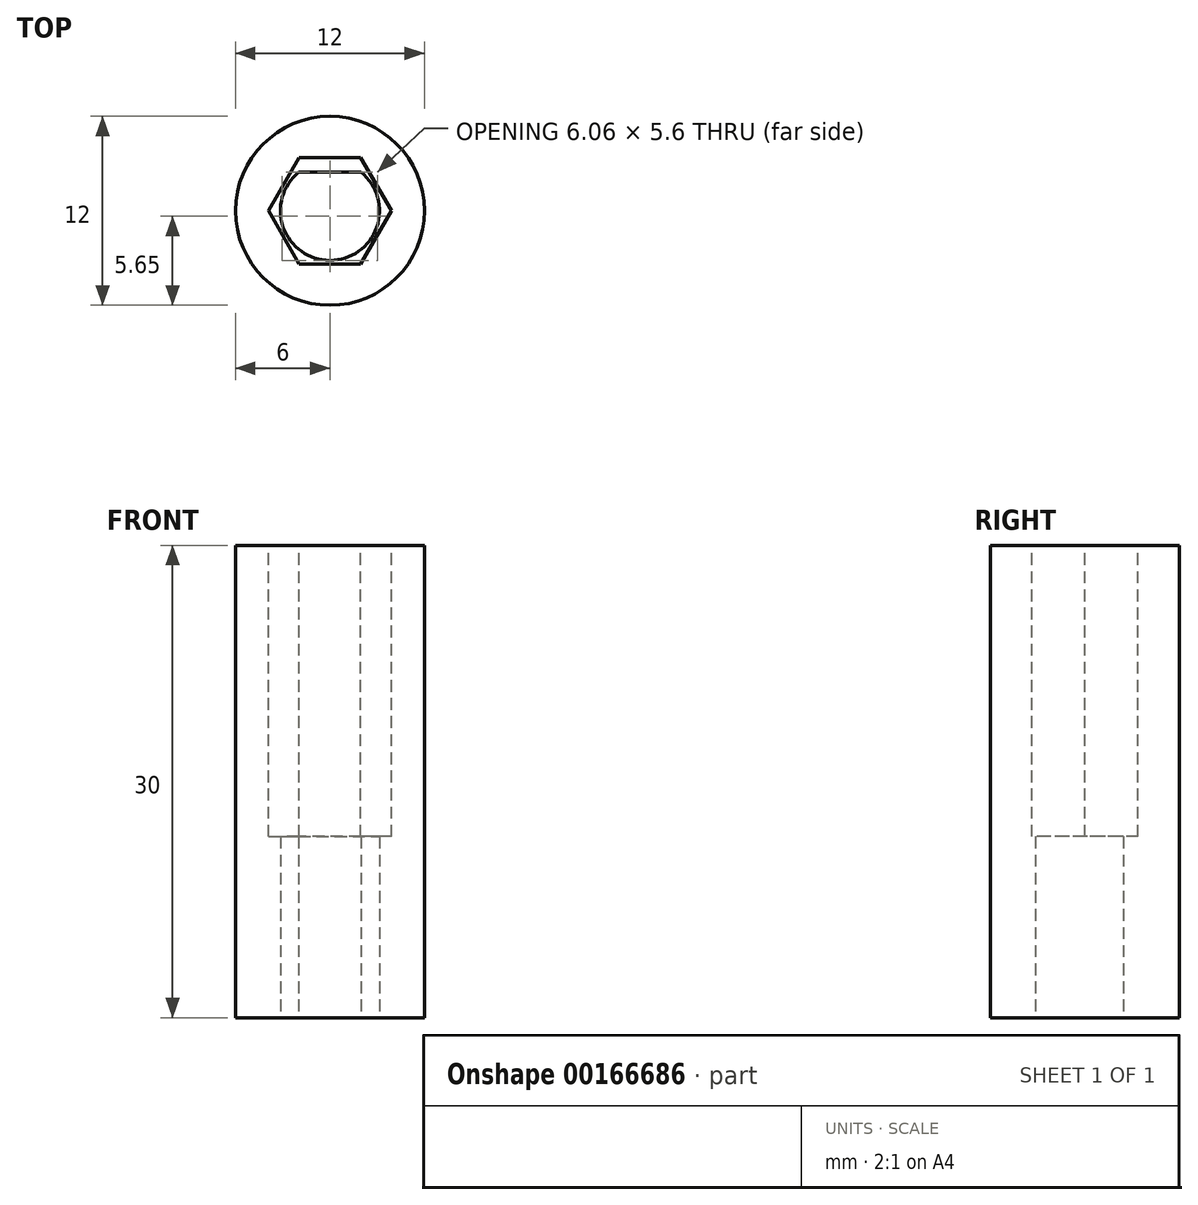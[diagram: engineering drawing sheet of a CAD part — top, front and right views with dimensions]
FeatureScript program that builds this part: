
annotation { "Feature Type Name" : "Feature", "Feature Type Description" : "" }
export const myFeature = defineFeature(function(context is Context, id is Id, definition is map)
    precondition{}
    {
        {
            var Q0;
            Q0=qCreatedBy(makeId("Top.planeOp"),FACE);
            var sketch = newSketch(context, id + "F0", { "sketchPlane" : qUnion([Q0])});
            skCircle(sketch, "E0", {"center": v(0, 0) * mm, "radius": 6 * mm});
            skSolve(sketch);
        }
        {
            var Q0;
            Q0 = qSketchRegion(id + "F0", true);
            extrude(context, id + "F1", {"entities" : qUnion([Q0]), "depth" : 30 * mm, "symmetric" : true});
        }
        {
            var Q0;
            Q0=makeQuery(id+"F1.opExtrude","CAP_FACE",FACE,{"disambiguationData":[OSD([sQuery(id+"F0.wireOp",EDGE,"E0")])],"isStart":true});
            var sketch = newSketch(context, id + "F2", { "sketchPlane" : qUnion([Q0])});
            skArc(sketch, "E1", {"start": v(1.98, -2.45) * mm, "mid": v(0, 3.15) * mm, "end": v(-1.98, -2.45) * mm});
            skLineSegment(sketch, "E2", {"start": v(-1.98, -2.45) * mm, "end": v(1.98, -2.45) * mm});
            skSolve(sketch);
        }
        {
            var Q0;
            Q0 = qSketchRegion(id + "F2", true);
            var Q1;
            Q1=sQuery(id+"F2.wireOp",EDGE,"E1");
            extrude(context, id + "F3", {"entities" : qUnion([Q0]), "operationType" : NewBodyOperationType.REMOVE, "surfaceEntities" : qUnion([Q1]), "oppositeDirection" : true, "depth" : 12 * mm});
        }
        {
            var Q0;
            Q0=makeQuery(id+"F1.opExtrude","CAP_FACE",FACE,{"disambiguationData":[OSD([sQuery(id+"F0.wireOp",EDGE,"E0")])],"isStart":false});
            var sketch = newSketch(context, id + "F4", { "sketchPlane" : qUnion([Q0])});
            skCircle(sketch, "E3.cCircle", {"center": v(0, 0) * mm, "radius": 3.38 * mm, "construction": true});
            skLineSegment(sketch, "E3.0", {"start": v(1.95, -3.38) * mm, "end": v(-1.95, -3.38) * mm});
            skLineSegment(sketch, "E3.1", {"start": v(-1.95, -3.38) * mm, "end": v(-3.9, 0) * mm});
            skLineSegment(sketch, "E3.2", {"start": v(-3.9, 0) * mm, "end": v(-1.95, 3.37) * mm});
            skLineSegment(sketch, "E3.3", {"start": v(-1.95, 3.37) * mm, "end": v(1.95, 3.38) * mm});
            skLineSegment(sketch, "E3.4", {"start": v(1.95, 3.38) * mm, "end": v(3.9, 0) * mm});
            skLineSegment(sketch, "E3.5", {"start": v(3.9, 0) * mm, "end": v(1.95, -3.38) * mm});
            skPoint(sketch, "E3.0.midPoint", {"position": v(0, -3.38) * mm});
            skSolve(sketch);
        }
        {
            var Q0;
            Q0 = qSketchRegion(id + "F4", true);
            extrude(context, id + "F5", {"entities" : qUnion([Q0]), "operationType" : NewBodyOperationType.REMOVE, "oppositeDirection" : true, "depth" : 18.5 * mm});
        }
    });
